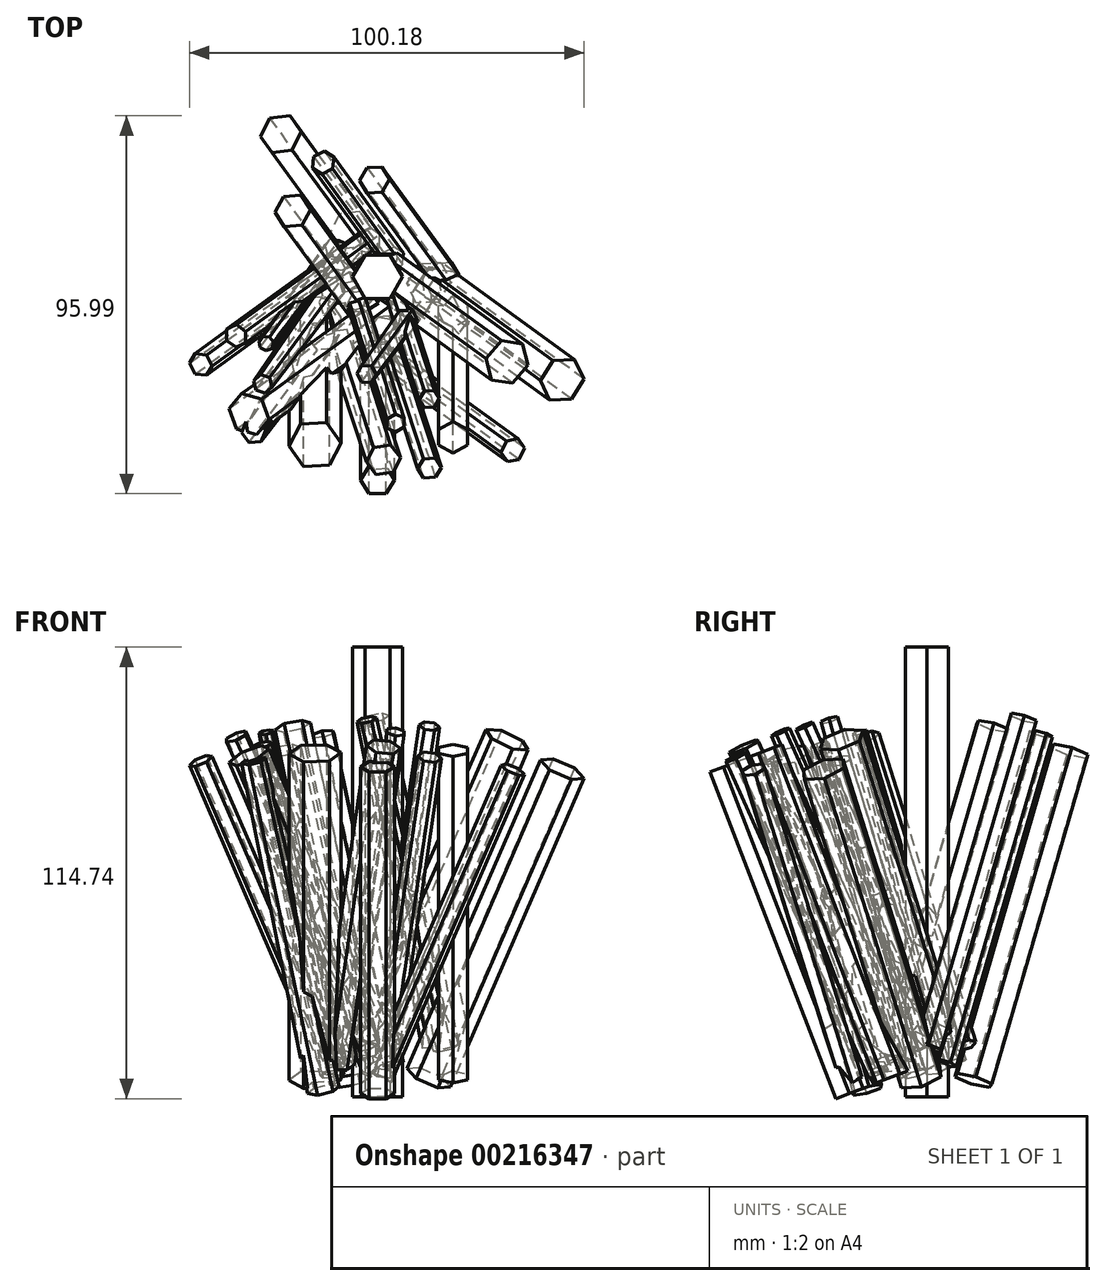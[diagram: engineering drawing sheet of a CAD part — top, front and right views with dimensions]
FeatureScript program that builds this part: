
annotation { "Feature Type Name" : "Feature", "Feature Type Description" : "" }
export const myFeature = defineFeature(function(context is Context, id is Id, definition is map)
    precondition{}
    {
        {
            var Q0;
            Q0=qCreatedBy(makeId("Top.planeOp"),FACE);
            cPlane(context, id + "F0", {"entities" : qUnion([Q0]), "cplaneType" : CPlaneType.OFFSET, "offset" : 17.78 * mm, "width" : 152.4 * mm, "height" : 152.4 * mm});
        }
        {
            var Q0;
            Q0=qCreatedBy(id+"F0.planeOp",FACE);
            var sketch = newSketch(context, id + "F1", { "sketchPlane" : qUnion([Q0])});
            skCircle(sketch, "E0.cCircle", {"center": v(0, 0) * mm, "radius": 39.09 * mm, "construction": true});
            skLineSegment(sketch, "E0.0", {"start": v(-12.7, 39.09) * mm, "end": v(12.7, 39.09) * mm, "construction": true});
            skLineSegment(sketch, "E0.1", {"start": v(12.7, 39.09) * mm, "end": v(33.25, 24.16) * mm, "construction": true});
            skLineSegment(sketch, "E0.2", {"start": v(33.25, 24.16) * mm, "end": v(41.1, 0) * mm, "construction": true});
            skLineSegment(sketch, "E0.3", {"start": v(41.1, 0) * mm, "end": v(33.25, -24.16) * mm, "construction": true});
            skLineSegment(sketch, "E0.4", {"start": v(33.25, -24.16) * mm, "end": v(12.7, -39.09) * mm, "construction": true});
            skLineSegment(sketch, "E0.5", {"start": v(12.7, -39.09) * mm, "end": v(-12.7, -39.09) * mm, "construction": true});
            skLineSegment(sketch, "E0.6", {"start": v(-12.7, -39.09) * mm, "end": v(-33.25, -24.16) * mm, "construction": true});
            skLineSegment(sketch, "E0.7", {"start": v(-33.25, -24.16) * mm, "end": v(-41.1, 0) * mm, "construction": true});
            skLineSegment(sketch, "E0.8", {"start": v(-41.1, 0) * mm, "end": v(-33.25, 24.16) * mm, "construction": true});
            skLineSegment(sketch, "E0.9", {"start": v(-33.25, 24.16) * mm, "end": v(-12.7, 39.09) * mm, "construction": true});
            skPoint(sketch, "E0.0.midPoint", {"position": v(0, 39.09) * mm});
            skSolve(sketch);
        }
        {
            var Q0;
            Q0=qCreatedBy(makeId("Top.planeOp"),FACE);
            var sketch = newSketch(context, id + "F2", { "sketchPlane" : qUnion([Q0])});
            skCircle(sketch, "E1.cCircle", {"center": v(0, 0) * mm, "radius": 22 * mm, "construction": true});
            skLineSegment(sketch, "E1.0", {"start": v(-12.7, 22) * mm, "end": v(12.7, 22) * mm, "construction": true});
            skLineSegment(sketch, "E1.1", {"start": v(12.7, 22) * mm, "end": v(25.4, 0) * mm, "construction": true});
            skLineSegment(sketch, "E1.2", {"start": v(25.4, 0) * mm, "end": v(12.7, -22) * mm, "construction": true});
            skLineSegment(sketch, "E1.3", {"start": v(12.7, -22) * mm, "end": v(-12.7, -22) * mm, "construction": true});
            skLineSegment(sketch, "E1.4", {"start": v(-12.7, -22) * mm, "end": v(-25.4, 0) * mm, "construction": true});
            skLineSegment(sketch, "E1.5", {"start": v(-25.4, 0) * mm, "end": v(-12.7, 22) * mm, "construction": true});
            skPoint(sketch, "E1.0.midPoint", {"position": v(0, 22) * mm});
            skSolve(sketch);
        }
        {
            var Q0;
            Q0=sQuery(id+"F1.wireOp",VERTEX,"E0.7.start");
            var Q1;
            Q1=sQuery(id+"F1.wireOp",VERTEX,"E0.1.start");
            var Q2;
            Q2=sQuery(id+"F2.wireOp",VERTEX,"E1.2.start");
            cPlane(context, id + "F3", {"entities" : qUnion([Q0, Q1, Q2]), "cplaneType" : CPlaneType.THREE_POINT, "offset" : 25.4 * mm, "width" : 152.4 * mm, "height" : 152.4 * mm});
        }
        {
            var Q0;
            Q0=sQuery(id+"F1.wireOp",VERTEX,"E0.8.start");
            var Q1;
            Q1=sQuery(id+"F1.wireOp",VERTEX,"E0.2.start");
            var Q2;
            Q2=sQuery(id+"F2.wireOp",VERTEX,"E1.3.start");
            cPlane(context, id + "F4", {"entities" : qUnion([Q0, Q1, Q2]), "cplaneType" : CPlaneType.THREE_POINT, "offset" : 25.4 * mm, "width" : 152.4 * mm, "height" : 152.4 * mm});
        }
        {
            var Q0;
            Q0=sQuery(id+"F1.wireOp",VERTEX,"E0.0.start");
            var Q1;
            Q1=sQuery(id+"F1.wireOp",VERTEX,"E0.2.end");
            var Q2;
            Q2=sQuery(id+"F2.wireOp",VERTEX,"E1.4.start");
            cPlane(context, id + "F5", {"entities" : qUnion([Q0, Q1, Q2]), "cplaneType" : CPlaneType.THREE_POINT, "offset" : 25.4 * mm, "width" : 152.4 * mm, "height" : 152.4 * mm});
        }
        {
            var Q0;
            Q0=sQuery(id+"F1.wireOp",VERTEX,"E0.4.start");
            var Q1;
            Q1=sQuery(id+"F1.wireOp",VERTEX,"E0.0.start");
            var Q2;
            Q2=sQuery(id+"F2.wireOp",VERTEX,"E1.5.start");
            cPlane(context, id + "F6", {"entities" : qUnion([Q0, Q1, Q2]), "cplaneType" : CPlaneType.THREE_POINT, "offset" : 25.4 * mm, "width" : 152.4 * mm, "height" : 152.4 * mm});
        }
        {
            var Q0;
            Q0=sQuery(id+"F1.wireOp",VERTEX,"E0.8.end");
            var Q1;
            Q1=sQuery(id+"F1.wireOp",VERTEX,"E0.2.start");
            var Q2;
            Q2=sQuery(id+"F2.wireOp",VERTEX,"E1.3.start");
            cPlane(context, id + "F7", {"entities" : qUnion([Q0, Q1, Q2]), "cplaneType" : CPlaneType.THREE_POINT, "offset" : 25.4 * mm, "width" : 152.4 * mm, "height" : 152.4 * mm});
        }
        {
            var Q0;
            Q0=sQuery(id+"F1.wireOp",VERTEX,"E0.6.start");
            var Q1;
            Q1=sQuery(id+"F1.wireOp",VERTEX,"E0.3.start");
            var Q2;
            Q2=sQuery(id+"F2.wireOp",VERTEX,"E1.5.end");
            cPlane(context, id + "F8", {"entities" : qUnion([Q0, Q1, Q2]), "cplaneType" : CPlaneType.THREE_POINT, "offset" : 25.4 * mm, "width" : 152.4 * mm, "height" : 152.4 * mm});
        }
        {
            var Q0;
            Q0=qCreatedBy(id+"F3.planeOp",FACE);
            var sketch = newSketch(context, id + "F9", { "sketchPlane" : qUnion([Q0])});
            skCircle(sketch, "E2.cCircle", {"center": v(-5.13, 6.55) * mm, "radius": 5.22 * mm, "construction": true});
            skLineSegment(sketch, "E2.0", {"start": v(-10.95, 8.11) * mm, "end": v(-6.69, 12.37) * mm});
            skLineSegment(sketch, "E2.1", {"start": v(-6.69, 12.37) * mm, "end": v(-0.86, 10.81) * mm});
            skLineSegment(sketch, "E2.2", {"start": v(-0.86, 10.81) * mm, "end": v(0.7, 4.99) * mm});
            skLineSegment(sketch, "E2.3", {"start": v(0.7, 4.99) * mm, "end": v(-3.57, 0.72) * mm});
            skLineSegment(sketch, "E2.4", {"start": v(-3.57, 0.72) * mm, "end": v(-9.4, 2.29) * mm});
            skLineSegment(sketch, "E2.5", {"start": v(-9.4, 2.29) * mm, "end": v(-10.95, 8.11) * mm});
            skPoint(sketch, "E2.0.midPoint", {"position": v(-8.82, 10.24) * mm});
            skCircle(sketch, "E3.cCircle", {"center": v(-3.57, -17.14) * mm, "radius": 2.78 * mm, "construction": true});
            skLineSegment(sketch, "E3.0", {"start": v(-5, -20) * mm, "end": v(-6.77, -17.32) * mm});
            skLineSegment(sketch, "E3.1", {"start": v(-6.77, -17.32) * mm, "end": v(-5.33, -14.45) * mm});
            skLineSegment(sketch, "E3.2", {"start": v(-5.33, -14.45) * mm, "end": v(-2.12, -14.27) * mm});
            skLineSegment(sketch, "E3.3", {"start": v(-2.12, -14.27) * mm, "end": v(-0.36, -16.95) * mm});
            skLineSegment(sketch, "E3.4", {"start": v(-0.36, -16.95) * mm, "end": v(-1.8, -19.82) * mm});
            skLineSegment(sketch, "E3.5", {"start": v(-1.8, -19.82) * mm, "end": v(-5, -20) * mm});
            skPoint(sketch, "E3.0.midPoint", {"position": v(-5.9, -18.67) * mm});
            skCircle(sketch, "E4.cCircle", {"center": v(10.03, 0) * mm, "radius": 5.2 * mm, "construction": true});
            skLineSegment(sketch, "E4.0", {"start": v(13.46, 4.94) * mm, "end": v(16.02, -0.5) * mm});
            skLineSegment(sketch, "E4.1", {"start": v(16.02, -0.5) * mm, "end": v(12.59, -5.44) * mm});
            skLineSegment(sketch, "E4.2", {"start": v(12.59, -5.44) * mm, "end": v(6.6, -4.94) * mm});
            skLineSegment(sketch, "E4.3", {"start": v(6.6, -4.94) * mm, "end": v(4.03, 0.5) * mm});
            skLineSegment(sketch, "E4.4", {"start": v(4.03, 0.5) * mm, "end": v(7.46, 5.44) * mm});
            skLineSegment(sketch, "E4.5", {"start": v(7.46, 5.44) * mm, "end": v(13.46, 4.94) * mm});
            skPoint(sketch, "E4.0.midPoint", {"position": v(14.74, 2.22) * mm});
            skSolve(sketch);
        }
        {
            var Q0;
            Q0 = qSketchRegion(id + "F9", true);
            extrude(context, id + "F10", {"entities" : qUnion([Q0]), "depth" : 88.9 * mm});
        }
        {
            var Q0;
            Q0=qCreatedBy(id+"F4.planeOp",FACE);
            var sketch = newSketch(context, id + "F11", { "sketchPlane" : qUnion([Q0])});
            skCircle(sketch, "E5.cCircle", {"center": v(-11.79, -5.88) * mm, "radius": 3.81 * mm, "construction": true});
            skLineSegment(sketch, "E5.0", {"start": v(-9.93, -1.9) * mm, "end": v(-7.4, -5.5) * mm});
            skLineSegment(sketch, "E5.1", {"start": v(-7.4, -5.5) * mm, "end": v(-9.26, -9.49) * mm});
            skLineSegment(sketch, "E5.2", {"start": v(-9.26, -9.49) * mm, "end": v(-13.65, -9.87) * mm});
            skLineSegment(sketch, "E5.3", {"start": v(-13.65, -9.87) * mm, "end": v(-16.17, -6.27) * mm});
            skLineSegment(sketch, "E5.4", {"start": v(-16.17, -6.27) * mm, "end": v(-14.31, -2.28) * mm});
            skLineSegment(sketch, "E5.5", {"start": v(-14.31, -2.28) * mm, "end": v(-9.93, -1.9) * mm});
            skPoint(sketch, "E5.0.midPoint", {"position": v(-8.67, -3.7) * mm});
            skCircle(sketch, "E6.cCircle", {"center": v(0, 10.32) * mm, "radius": 2.27 * mm, "construction": true});
            skLineSegment(sketch, "E6.0", {"start": v(-1.3, 12.59) * mm, "end": v(1.3, 12.59) * mm});
            skLineSegment(sketch, "E6.1", {"start": v(1.3, 12.59) * mm, "end": v(2.62, 10.32) * mm});
            skLineSegment(sketch, "E6.2", {"start": v(2.62, 10.32) * mm, "end": v(1.3, 8.06) * mm});
            skLineSegment(sketch, "E6.3", {"start": v(1.3, 8.06) * mm, "end": v(-1.3, 8.06) * mm});
            skLineSegment(sketch, "E6.4", {"start": v(-1.3, 8.06) * mm, "end": v(-2.62, 10.32) * mm});
            skLineSegment(sketch, "E6.5", {"start": v(-2.62, 10.32) * mm, "end": v(-1.3, 12.59) * mm});
            skPoint(sketch, "E6.0.midPoint", {"position": v(0, 12.59) * mm});
            skCircle(sketch, "E7.cCircle", {"center": v(0, -8.87) * mm, "radius": 2.65 * mm, "construction": true});
            skLineSegment(sketch, "E7.0", {"start": v(-1.53, -6.22) * mm, "end": v(1.53, -6.22) * mm});
            skLineSegment(sketch, "E7.1", {"start": v(1.53, -6.22) * mm, "end": v(3.06, -8.87) * mm});
            skLineSegment(sketch, "E7.2", {"start": v(3.06, -8.87) * mm, "end": v(1.53, -11.52) * mm});
            skLineSegment(sketch, "E7.3", {"start": v(1.53, -11.52) * mm, "end": v(-1.53, -11.52) * mm});
            skLineSegment(sketch, "E7.4", {"start": v(-1.53, -11.52) * mm, "end": v(-3.06, -8.87) * mm});
            skLineSegment(sketch, "E7.5", {"start": v(-3.06, -8.87) * mm, "end": v(-1.53, -6.22) * mm});
            skPoint(sketch, "E7.0.midPoint", {"position": v(0, -6.22) * mm});
            skCircle(sketch, "E8.cCircle", {"center": v(-8.67, 4.15) * mm, "radius": 2.2 * mm, "construction": true});
            skLineSegment(sketch, "E8.0", {"start": v(-10.86, 2.88) * mm, "end": v(-10.86, 5.42) * mm});
            skLineSegment(sketch, "E8.1", {"start": v(-10.86, 5.42) * mm, "end": v(-8.67, 6.69) * mm});
            skLineSegment(sketch, "E8.2", {"start": v(-8.67, 6.69) * mm, "end": v(-6.47, 5.42) * mm});
            skLineSegment(sketch, "E8.3", {"start": v(-6.47, 5.42) * mm, "end": v(-6.47, 2.88) * mm});
            skLineSegment(sketch, "E8.4", {"start": v(-6.47, 2.88) * mm, "end": v(-8.67, 1.61) * mm});
            skLineSegment(sketch, "E8.5", {"start": v(-8.67, 1.61) * mm, "end": v(-10.86, 2.88) * mm});
            skPoint(sketch, "E8.0.midPoint", {"position": v(-10.86, 4.15) * mm});
            skSolve(sketch);
        }
        {
            var Q0;
            Q0 = qSketchRegion(id + "F11", true);
            extrude(context, id + "F12", {"entities" : qUnion([Q0]), "operationType" : NewBodyOperationType.ADD, "depth" : 88.9 * mm});
        }
        {
            var Q0;
            Q0=qCreatedBy(makeId("Top.planeOp"),FACE);
            var sketch = newSketch(context, id + "F13", { "sketchPlane" : qUnion([Q0])});
            skCircle(sketch, "E9.cCircle", {"center": v(0, 0) * mm, "radius": 5.5 * mm, "construction": true});
            skLineSegment(sketch, "E9.0", {"start": v(-3.17, 5.5) * mm, "end": v(3.17, 5.5) * mm});
            skLineSegment(sketch, "E9.1", {"start": v(3.18, 5.5) * mm, "end": v(6.35, 0) * mm});
            skLineSegment(sketch, "E9.2", {"start": v(6.35, 0) * mm, "end": v(3.18, -5.5) * mm});
            skLineSegment(sketch, "E9.3", {"start": v(3.18, -5.5) * mm, "end": v(-3.17, -5.5) * mm});
            skLineSegment(sketch, "E9.4", {"start": v(-3.17, -5.5) * mm, "end": v(-6.35, 0) * mm});
            skLineSegment(sketch, "E9.5", {"start": v(-6.35, 0) * mm, "end": v(-3.17, 5.5) * mm});
            skPoint(sketch, "E9.0.midPoint", {"position": v(0, 5.5) * mm});
            skSolve(sketch);
        }
        {
            var Q0;
            Q0 = qSketchRegion(id + "F13", true);
            extrude(context, id + "F14", {"entities" : qUnion([Q0]), "operationType" : NewBodyOperationType.ADD, "depth" : 114.3 * mm});
        }
        {
            var Q0;
            Q0=qCreatedBy(id+"F5.planeOp",FACE);
            var sketch = newSketch(context, id + "F15", { "sketchPlane" : qUnion([Q0])});
            skCircle(sketch, "E10.cCircle", {"center": v(-9.99, -1.17) * mm, "radius": 2.92 * mm, "construction": true});
            skLineSegment(sketch, "E10.0", {"start": v(-13.24, -0.3) * mm, "end": v(-10.86, 2.08) * mm});
            skLineSegment(sketch, "E10.1", {"start": v(-10.86, 2.08) * mm, "end": v(-7.6, 1.21) * mm});
            skLineSegment(sketch, "E10.2", {"start": v(-7.6, 1.21) * mm, "end": v(-6.74, -2.04) * mm});
            skLineSegment(sketch, "E10.3", {"start": v(-6.74, -2.04) * mm, "end": v(-9.12, -4.42) * mm});
            skLineSegment(sketch, "E10.4", {"start": v(-9.12, -4.42) * mm, "end": v(-12.37, -3.55) * mm});
            skLineSegment(sketch, "E10.5", {"start": v(-12.37, -3.55) * mm, "end": v(-13.24, -0.3) * mm});
            skPoint(sketch, "E10.0.midPoint", {"position": v(-12.05, 0.9) * mm});
            skCircle(sketch, "E11.cCircle", {"center": v(-12.37, -13.93) * mm, "radius": 3.54 * mm, "construction": true});
            skLineSegment(sketch, "E11.0", {"start": v(-16.42, -14.5) * mm, "end": v(-14.9, -10.71) * mm});
            skLineSegment(sketch, "E11.1", {"start": v(-14.9, -10.71) * mm, "end": v(-10.84, -10.14) * mm});
            skLineSegment(sketch, "E11.2", {"start": v(-10.84, -10.14) * mm, "end": v(-8.32, -13.36) * mm});
            skLineSegment(sketch, "E11.3", {"start": v(-8.32, -13.36) * mm, "end": v(-9.85, -17.15) * mm});
            skLineSegment(sketch, "E11.4", {"start": v(-9.85, -17.15) * mm, "end": v(-13.9, -17.73) * mm});
            skLineSegment(sketch, "E11.5", {"start": v(-13.9, -17.73) * mm, "end": v(-16.42, -14.5) * mm});
            skPoint(sketch, "E11.0.midPoint", {"position": v(-15.66, -12.6) * mm});
            skCircle(sketch, "E12.cCircle", {"center": v(-9.12, 9.6) * mm, "radius": 2.52 * mm, "construction": true});
            skLineSegment(sketch, "E12.0", {"start": v(-10.33, 12.12) * mm, "end": v(-7.9, 12.12) * mm});
            skLineSegment(sketch, "E12.1", {"start": v(-7.9, 12.12) * mm, "end": v(-6.39, 10.22) * mm});
            skLineSegment(sketch, "E12.2", {"start": v(-6.39, 10.22) * mm, "end": v(-6.93, 7.85) * mm});
            skLineSegment(sketch, "E12.3", {"start": v(-6.93, 7.85) * mm, "end": v(-9.12, 6.8) * mm});
            skLineSegment(sketch, "E12.4", {"start": v(-9.12, 6.8) * mm, "end": v(-11.3, 7.85) * mm});
            skLineSegment(sketch, "E12.5", {"start": v(-11.3, 7.85) * mm, "end": v(-11.85, 10.22) * mm});
            skLineSegment(sketch, "E12.6", {"start": v(-11.85, 10.22) * mm, "end": v(-10.33, 12.12) * mm});
            skPoint(sketch, "E12.0.midPoint", {"position": v(-9.12, 12.12) * mm});
            skCircle(sketch, "E13.cCircle", {"center": v(16.94, 3) * mm, "radius": 2.99 * mm, "construction": true});
            skLineSegment(sketch, "E13.0", {"start": v(18.68, 0) * mm, "end": v(15.23, 0) * mm});
            skLineSegment(sketch, "E13.1", {"start": v(15.23, 0) * mm, "end": v(13.5, 2.98) * mm});
            skLineSegment(sketch, "E13.2", {"start": v(13.5, 2.98) * mm, "end": v(15.21, 5.97) * mm});
            skLineSegment(sketch, "E13.3", {"start": v(15.21, 5.97) * mm, "end": v(18.66, 5.98) * mm});
            skLineSegment(sketch, "E13.4", {"start": v(18.66, 5.98) * mm, "end": v(20.4, 3) * mm});
            skLineSegment(sketch, "E13.5", {"start": v(20.4, 3) * mm, "end": v(18.68, 0) * mm});
            skPoint(sketch, "E13.0.midPoint", {"position": v(16.95, 0) * mm});
            skSolve(sketch);
        }
        {
            var Q0;
            Q0 = qSketchRegion(id + "F15", true);
            extrude(context, id + "F16", {"entities" : qUnion([Q0]), "operationType" : NewBodyOperationType.ADD, "depth" : 88.9 * mm, "hasDraft" : true, "draftAngle" : .5 * degree, "draftPullDirection" : true});
        }
        {
            var Q0;
            Q0=qCreatedBy(id+"F6.planeOp",FACE);
            var sketch = newSketch(context, id + "F17", { "sketchPlane" : qUnion([Q0])});
            skCircle(sketch, "E14.cCircle", {"center": v(-7.87, -4.34) * mm, "radius": 2.7 * mm, "construction": true});
            skLineSegment(sketch, "E14.0", {"start": v(-6.31, -7.03) * mm, "end": v(-9.42, -7.03) * mm});
            skLineSegment(sketch, "E14.1", {"start": v(-9.42, -7.03) * mm, "end": v(-10.98, -4.34) * mm});
            skLineSegment(sketch, "E14.2", {"start": v(-10.98, -4.34) * mm, "end": v(-9.42, -1.65) * mm});
            skLineSegment(sketch, "E14.3", {"start": v(-9.42, -1.65) * mm, "end": v(-6.31, -1.65) * mm});
            skLineSegment(sketch, "E14.4", {"start": v(-6.31, -1.65) * mm, "end": v(-4.76, -4.34) * mm});
            skLineSegment(sketch, "E14.5", {"start": v(-4.76, -4.34) * mm, "end": v(-6.31, -7.03) * mm});
            skPoint(sketch, "E14.0.midPoint", {"position": v(-7.87, -7.03) * mm});
            skCircle(sketch, "E15.cCircle", {"center": v(1.84, -13.07) * mm, "radius": 2.61 * mm, "construction": true});
            skLineSegment(sketch, "E15.0", {"start": v(4.46, -14.58) * mm, "end": v(1.85, -16.09) * mm});
            skLineSegment(sketch, "E15.1", {"start": v(1.85, -16.09) * mm, "end": v(-0.77, -14.58) * mm});
            skLineSegment(sketch, "E15.2", {"start": v(-0.77, -14.58) * mm, "end": v(-0.77, -11.57) * mm});
            skLineSegment(sketch, "E15.3", {"start": v(-0.77, -11.57) * mm, "end": v(1.84, -10.06) * mm});
            skLineSegment(sketch, "E15.4", {"start": v(1.84, -10.06) * mm, "end": v(4.45, -11.56) * mm});
            skLineSegment(sketch, "E15.5", {"start": v(4.45, -11.56) * mm, "end": v(4.46, -14.58) * mm});
            skPoint(sketch, "E15.0.midPoint", {"position": v(3.15, -15.33) * mm});
            skCircle(sketch, "E16.cCircle", {"center": v(5.31, 7.3) * mm, "radius": 4.81 * mm, "construction": true});
            skLineSegment(sketch, "E16.0", {"start": v(10.8, 8.13) * mm, "end": v(8.77, 2.96) * mm});
            skLineSegment(sketch, "E16.1", {"start": v(8.77, 2.96) * mm, "end": v(3.28, 2.13) * mm});
            skLineSegment(sketch, "E16.2", {"start": v(3.28, 2.13) * mm, "end": v(-0.18, 6.48) * mm});
            skLineSegment(sketch, "E16.3", {"start": v(-0.18, 6.48) * mm, "end": v(1.85, 11.65) * mm});
            skLineSegment(sketch, "E16.4", {"start": v(1.85, 11.65) * mm, "end": v(7.35, 12.47) * mm});
            skLineSegment(sketch, "E16.5", {"start": v(7.35, 12.47) * mm, "end": v(10.8, 8.13) * mm});
            skPoint(sketch, "E16.0.midPoint", {"position": v(9.8, 5.54) * mm});
            skSolve(sketch);
        }
        {
            var Q0;
            Q0 = qSketchRegion(id + "F17", true);
            extrude(context, id + "F18", {"entities" : qUnion([Q0]), "operationType" : NewBodyOperationType.ADD, "oppositeDirection" : true, "depth" : 88.9 * mm});
        }
        {
            var Q0;
            Q0=qCreatedBy(id+"F7.planeOp",FACE);
            var sketch = newSketch(context, id + "F19", { "sketchPlane" : qUnion([Q0])});
            skCircle(sketch, "E17.cCircle", {"center": v(0, -18.03) * mm, "radius": 3.73 * mm, "construction": true});
            skLineSegment(sketch, "E17.0", {"start": v(-2.15, -14.3) * mm, "end": v(2.15, -14.3) * mm});
            skLineSegment(sketch, "E17.1", {"start": v(2.15, -14.3) * mm, "end": v(4.3, -18.03) * mm});
            skLineSegment(sketch, "E17.2", {"start": v(4.3, -18.03) * mm, "end": v(2.15, -21.76) * mm});
            skLineSegment(sketch, "E17.3", {"start": v(2.15, -21.76) * mm, "end": v(-2.15, -21.76) * mm});
            skLineSegment(sketch, "E17.4", {"start": v(-2.15, -21.76) * mm, "end": v(-4.3, -18.03) * mm});
            skLineSegment(sketch, "E17.5", {"start": v(-4.3, -18.03) * mm, "end": v(-2.15, -14.3) * mm});
            skPoint(sketch, "E17.0.midPoint", {"position": v(0, -14.3) * mm});
            skCircle(sketch, "E18.cCircle", {"center": v(19.15, -6.42) * mm, "radius": 3.73 * mm, "construction": true});
            skLineSegment(sketch, "E18.0", {"start": v(22.88, -4.27) * mm, "end": v(22.88, -8.57) * mm});
            skLineSegment(sketch, "E18.1", {"start": v(22.88, -8.57) * mm, "end": v(19.15, -10.73) * mm});
            skLineSegment(sketch, "E18.2", {"start": v(19.15, -10.73) * mm, "end": v(15.42, -8.57) * mm});
            skLineSegment(sketch, "E18.3", {"start": v(15.42, -8.57) * mm, "end": v(15.42, -4.27) * mm});
            skLineSegment(sketch, "E18.4", {"start": v(15.42, -4.27) * mm, "end": v(19.15, -2.11) * mm});
            skLineSegment(sketch, "E18.5", {"start": v(19.15, -2.11) * mm, "end": v(22.88, -4.27) * mm});
            skPoint(sketch, "E18.0.midPoint", {"position": v(22.88, -6.42) * mm});
            skCircle(sketch, "E19.cCircle", {"center": v(-15.89, -8.4) * mm, "radius": 5.76 * mm, "construction": true});
            skLineSegment(sketch, "E19.0", {"start": v(-12.17, -13.93) * mm, "end": v(-9.25, -7.95) * mm});
            skLineSegment(sketch, "E19.1", {"start": v(-18.8, -14.38) * mm, "end": v(-12.17, -13.93) * mm});
            skLineSegment(sketch, "E19.2", {"start": v(-22.52, -8.86) * mm, "end": v(-18.8, -14.38) * mm});
            skLineSegment(sketch, "E19.3", {"start": v(-19.6, -2.89) * mm, "end": v(-22.52, -8.86) * mm});
            skLineSegment(sketch, "E19.4", {"start": v(-12.97, -2.43) * mm, "end": v(-19.6, -2.89) * mm});
            skLineSegment(sketch, "E19.5", {"start": v(-9.25, -7.95) * mm, "end": v(-12.97, -2.43) * mm});
            skPoint(sketch, "E19.0.midPoint", {"position": v(-10.71, -10.94) * mm});
            skSolve(sketch);
        }
        {
            var Q0;
            Q0 = qSketchRegion(id + "F19", true);
            extrude(context, id + "F20", {"entities" : qUnion([Q0]), "operationType" : NewBodyOperationType.ADD, "depth" : 88.9 * mm});
        }
        {
            var Q0;
            Q0=qCreatedBy(id+"F8.planeOp",FACE);
            var sketch = newSketch(context, id + "F21", { "sketchPlane" : qUnion([Q0])});
            skCircle(sketch, "E20.cCircle", {"center": v(-5.27, -10.23) * mm, "radius": 4.57 * mm, "construction": true});
            skLineSegment(sketch, "E20.0", {"start": v(0, -10.57) * mm, "end": v(-2.93, -14.96) * mm});
            skLineSegment(sketch, "E20.1", {"start": v(-2.93, -14.96) * mm, "end": v(-8.2, -14.62) * mm});
            skLineSegment(sketch, "E20.2", {"start": v(-8.2, -14.62) * mm, "end": v(-10.54, -9.88) * mm});
            skLineSegment(sketch, "E20.3", {"start": v(-10.54, -9.88) * mm, "end": v(-7.6, -5.5) * mm});
            skLineSegment(sketch, "E20.4", {"start": v(-7.6, -5.5) * mm, "end": v(-2.33, -5.84) * mm});
            skLineSegment(sketch, "E20.5", {"start": v(-2.33, -5.84) * mm, "end": v(0, -10.57) * mm});
            skPoint(sketch, "E20.0.midPoint", {"position": v(-1.47, -12.77) * mm});
            skCircle(sketch, "E21.cCircle", {"center": v(18.98, 3.29) * mm, "radius": 3.32 * mm, "construction": true});
            skLineSegment(sketch, "E21.0", {"start": v(17.06, 6.6) * mm, "end": v(20.9, 6.6) * mm});
            skLineSegment(sketch, "E21.1", {"start": v(20.9, 6.6) * mm, "end": v(22.82, 3.29) * mm});
            skLineSegment(sketch, "E21.2", {"start": v(22.82, 3.29) * mm, "end": v(20.9, -0.04) * mm});
            skLineSegment(sketch, "E21.3", {"start": v(20.9, -0.04) * mm, "end": v(17.06, -0.04) * mm});
            skLineSegment(sketch, "E21.4", {"start": v(17.06, -0.04) * mm, "end": v(15.15, 3.29) * mm});
            skLineSegment(sketch, "E21.5", {"start": v(15.15, 3.29) * mm, "end": v(17.06, 6.6) * mm});
            skPoint(sketch, "E21.0.midPoint", {"position": v(18.98, 6.6) * mm});
            skCircle(sketch, "E22.cCircle", {"center": v(-2.22, 10.26) * mm, "radius": 3.98 * mm, "construction": true});
            skLineSegment(sketch, "E22.0", {"start": v(0.18, 14.18) * mm, "end": v(2.37, 10.14) * mm});
            skLineSegment(sketch, "E22.1", {"start": v(2.37, 10.14) * mm, "end": v(-0.03, 6.22) * mm});
            skLineSegment(sketch, "E22.2", {"start": v(-0.03, 6.22) * mm, "end": v(-4.62, 6.34) * mm});
            skLineSegment(sketch, "E22.3", {"start": v(-4.62, 6.34) * mm, "end": v(-6.81, 10.38) * mm});
            skLineSegment(sketch, "E22.4", {"start": v(-6.81, 10.38) * mm, "end": v(-4.41, 14.3) * mm});
            skLineSegment(sketch, "E22.5", {"start": v(-4.41, 14.3) * mm, "end": v(0.18, 14.18) * mm});
            skPoint(sketch, "E22.0.midPoint", {"position": v(1.28, 12.16) * mm});
            skCircle(sketch, "E23.cCircle", {"center": v(5.68, -2.05) * mm, "radius": 2.61 * mm, "construction": true});
            skLineSegment(sketch, "E23.0", {"start": v(8.43, -3.3) * mm, "end": v(5.97, -5.06) * mm});
            skLineSegment(sketch, "E23.1", {"start": v(5.97, -5.06) * mm, "end": v(3.23, -3.8) * mm});
            skLineSegment(sketch, "E23.2", {"start": v(3.23, -3.8) * mm, "end": v(2.94, -0.8) * mm});
            skLineSegment(sketch, "E23.3", {"start": v(2.94, -0.8) * mm, "end": v(5.4, 0.95) * mm});
            skLineSegment(sketch, "E23.4", {"start": v(5.4, 0.95) * mm, "end": v(8.14, -0.3) * mm});
            skLineSegment(sketch, "E23.5", {"start": v(8.14, -0.3) * mm, "end": v(8.43, -3.3) * mm});
            skPoint(sketch, "E23.0.midPoint", {"position": v(7.2, -4.18) * mm});
            skSolve(sketch);
        }
        {
            var Q0;
            Q0 = qSketchRegion(id + "F21", true);
            extrude(context, id + "F22", {"entities" : qUnion([Q0]), "operationType" : NewBodyOperationType.ADD, "oppositeDirection" : true, "depth" : 88.9 * mm});
        }
        {
            var Q0;
            Q0=qCreatedBy(makeId("Top.planeOp"),FACE);
            cPlane(context, id + "F24", {"entities" : qUnion([Q0]), "cplaneType" : CPlaneType.OFFSET, "offset" : 25.4 * mm, "width" : 152.4 * mm, "height" : 152.4 * mm});
        }
    });
